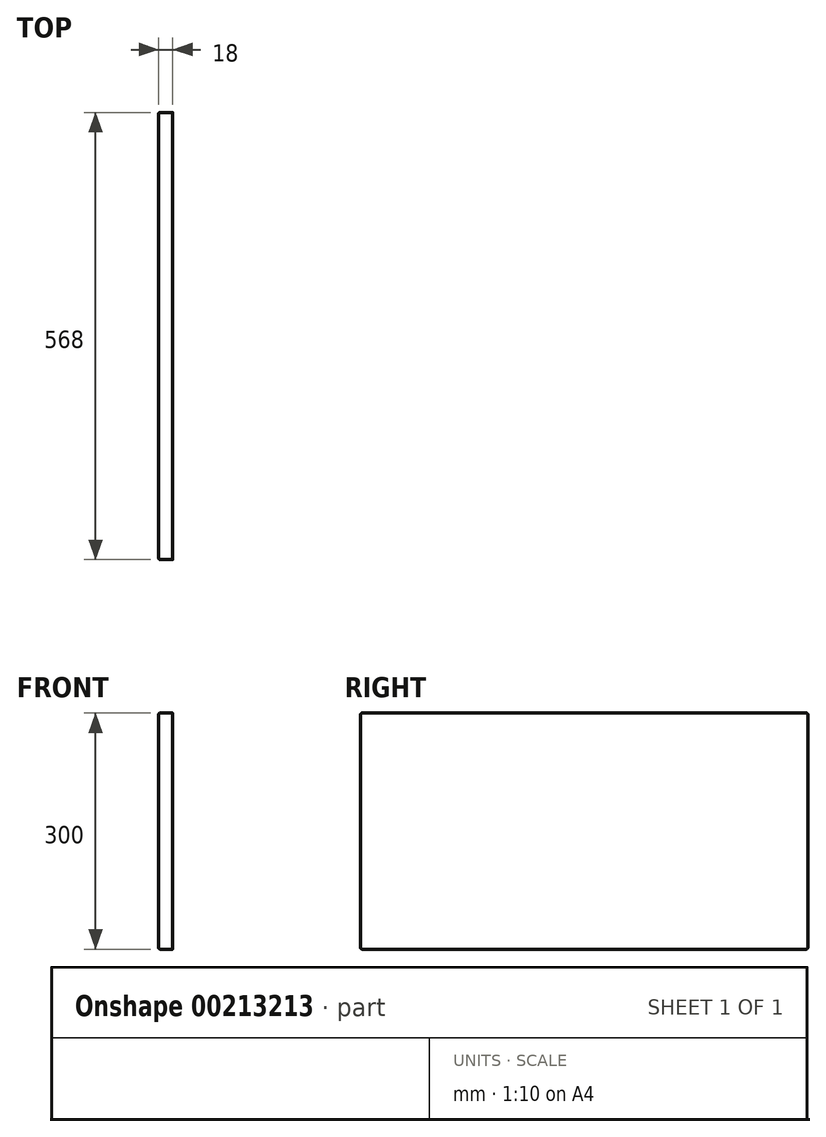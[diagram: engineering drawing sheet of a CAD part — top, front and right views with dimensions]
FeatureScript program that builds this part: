
annotation { "Feature Type Name" : "Feature", "Feature Type Description" : "" }
export const myFeature = defineFeature(function(context is Context, id is Id, definition is map)
    precondition{}
    {
        {
            var Q0;
            Q0=qCreatedBy(makeId("Right.planeOp"),FACE);
            var sketch = newSketch(context, id + "F0", { "sketchPlane" : qUnion([Q0])});
            skLineSegment(sketch, "E0.bottom", {"start": v(-284, 150) * mm, "end": v(284, 150) * mm});
            skLineSegment(sketch, "E0.top", {"start": v(-284, -150) * mm, "end": v(284, -150) * mm});
            skLineSegment(sketch, "E0.left", {"start": v(-284, 150) * mm, "end": v(-284, -150) * mm});
            skLineSegment(sketch, "E0.right", {"start": v(284, 150) * mm, "end": v(284, -150) * mm});
            skPoint(sketch, "E0.middle", {"position": v(0, 0) * mm});
            skSolve(sketch);
        }
        {
            var Q0;
            Q0=makeQuery(id+"F0.imprint","IMPRINT",FACE,{"disambiguationData":[TD([[makeQuery(id+"F0.imprint","IMPRINT",EDGE,{"derivedFrom":sQuery(id+"F0.wireOp",EDGE,"E0.bottom")}),-1.0]])]});
            extrude(context, id + "F1", {"entities" : qUnion([Q0]), "endBound" : BoundingType.SYMMETRIC, "depth" : 18 * mm});
        }
        {
            var Q0;
            Q0=makeQuery(id+"F1.opExtrude","CAP_FACE",FACE,{"disambiguationData":[OSD([sQuery(id+"F0.wireOp",EDGE,"E0.bottom"),sQuery(id+"F0.wireOp",EDGE,"E0.top"),sQuery(id+"F0.wireOp",EDGE,"E0.left"),sQuery(id+"F0.wireOp",EDGE,"E0.right")])],"isStart":true});
            var Q1;
            Q1=makeQuery(id+"F1.opExtrude","SWEPT_EDGE",EDGE,{"disambiguationData":[OSD([sQuery(id+"F0.wireOp",EDGE,"E0.bottom"),sQuery(id+"F0.wireOp",EDGE,"E0.right")])]});
            var Q2;
            Q2=makeQuery(id+"F1.opExtrude","SWEPT_EDGE",EDGE,{"disambiguationData":[OSD([sQuery(id+"F0.wireOp",EDGE,"E0.top"),sQuery(id+"F0.wireOp",EDGE,"E0.right")])]});
            var Q3;
            Q3=makeQuery(id+"F1.opExtrude","SWEPT_EDGE",EDGE,{"disambiguationData":[OSD([sQuery(id+"F0.wireOp",EDGE,"E0.bottom"),sQuery(id+"F0.wireOp",EDGE,"E0.left")])]});
            var Q4;
            Q4=makeQuery(id+"F1.opExtrude","SWEPT_EDGE",EDGE,{"disambiguationData":[OSD([sQuery(id+"F0.wireOp",EDGE,"E0.top"),sQuery(id+"F0.wireOp",EDGE,"E0.left")])]});
            fillet(context, id + "F2", {"entities" : qUnion([Q0, Q1, Q2, Q3, Q4]), "radius" : 2 * mm, "tangentPropagation" : true, "allowEdgeOverflow" : false});
        }
    });
